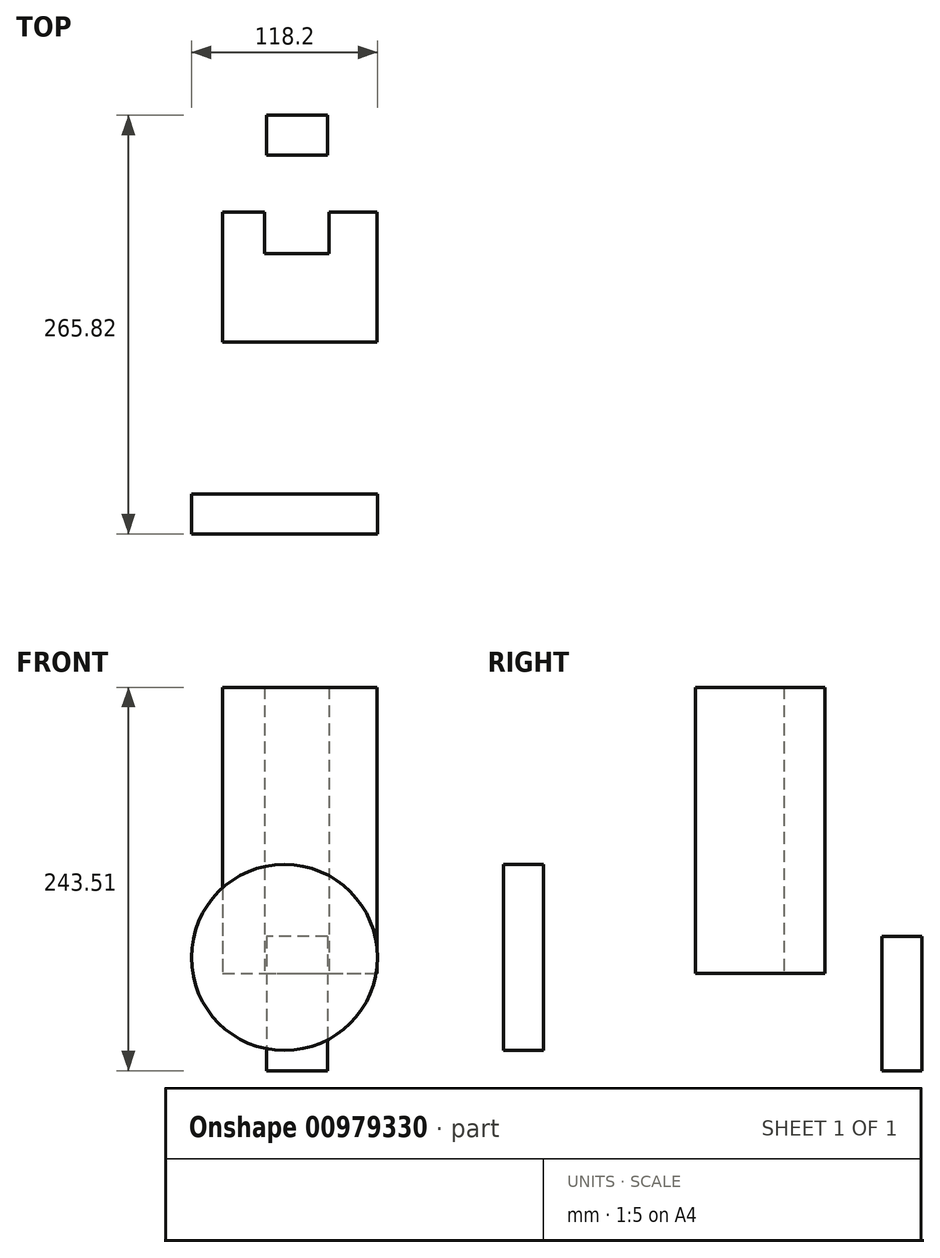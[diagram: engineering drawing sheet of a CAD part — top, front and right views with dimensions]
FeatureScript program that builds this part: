
annotation { "Feature Type Name" : "Feature", "Feature Type Description" : "" }
export const myFeature = defineFeature(function(context is Context, id is Id, definition is map)
    precondition{}
    {
        {
            var Q0;
            Q0=qCreatedBy(makeId("Top.planeOp"),FACE);
            var sketch = newSketch(context, id + "F0", { "sketchPlane" : qUnion([Q0])});
            skLineSegment(sketch, "E0.bottom", {"start": v(-39.24, 38.4) * mm, "end": v(58.8, 38.4) * mm});
            skLineSegment(sketch, "E0.top", {"start": v(-39.24, -43.86) * mm, "end": v(58.8, -43.86) * mm});
            skLineSegment(sketch, "E0.left", {"start": v(-39.24, 38.4) * mm, "end": v(-39.24, -43.86) * mm});
            skLineSegment(sketch, "E0.right", {"start": v(58.8, 38.4) * mm, "end": v(58.8, -43.86) * mm});
            skLineSegment(sketch, "E1.bottom", {"start": v(-12.7, 38.4) * mm, "end": v(28.15, 38.4) * mm});
            skLineSegment(sketch, "E1.top", {"start": v(-12.7, 12.3) * mm, "end": v(28.15, 12.3) * mm});
            skLineSegment(sketch, "E1.left", {"start": v(-12.7, 38.4) * mm, "end": v(-12.7, 12.3) * mm});
            skLineSegment(sketch, "E1.right", {"start": v(28.15, 38.4) * mm, "end": v(28.15, 12.3) * mm});
            skSolve(sketch);
        }
        {
            var Q0;
            Q0=makeQuery(id+"F0.imprint","IMPRINT",FACE,{"disambiguationData":[TD([[makeQuery(id+"F0.imprint","IMPRINT",EDGE,{"derivedFrom":sQuery(id+"F0.wireOp",EDGE,"E0.top")}),1.0]])]});
            extrude(context, id + "F1", {"entities" : qUnion([Q0]), "depth" : 181.6 * mm, "offsetDistance" : 25.4 * mm});
        }
        {
            var Q0;
            Q0=qCreatedBy(makeId("Front.planeOp"),FACE);
            cPlane(context, id + "F2", {"entities" : qUnion([Q0]), "cplaneType" : CPlaneType.OFFSET, "offset" : 100.02 * mm, "oppositeDirection" : true, "width" : 152.4 * mm, "height" : 152.4 * mm});
        }
        {
            var Q0;
            Q0=qCreatedBy(id+"F2.planeOp",FACE);
            var sketch = newSketch(context, id + "F3", { "sketchPlane" : qUnion([Q0])});
            skLineSegment(sketch, "E2.bottom", {"start": v(27.2, 23.32) * mm, "end": v(-11.26, 23.32) * mm});
            skLineSegment(sketch, "E2.top", {"start": v(27.2, -61.9) * mm, "end": v(-11.26, -61.9) * mm});
            skLineSegment(sketch, "E2.left", {"start": v(27.2, 23.32) * mm, "end": v(27.2, -61.9) * mm});
            skLineSegment(sketch, "E2.right", {"start": v(-11.26, 23.32) * mm, "end": v(-11.26, -61.9) * mm});
            skSolve(sketch);
        }
        {
            var Q0;
            Q0=makeQuery(id+"F3.imprint","IMPRINT",FACE,{"disambiguationData":[TD([[makeQuery(id+"F3.imprint","IMPRINT",EDGE,{"derivedFrom":sQuery(id+"F3.wireOp",EDGE,"E2.bottom")}),1.0]])]});
            extrude(context, id + "F4", {"entities" : qUnion([Q0]), "depth" : 25.4 * mm, "offsetDistance" : 25.4 * mm});
        }
        {
            var Q0;
            Q0=qCreatedBy(makeId("Front.planeOp"),FACE);
            cPlane(context, id + "F5", {"entities" : qUnion([Q0]), "cplaneType" : CPlaneType.OFFSET, "offset" : 140.4 * mm, "width" : 152.4 * mm, "height" : 152.4 * mm});
        }
        {
            var Q0;
            Q0=qCreatedBy(id+"F5.planeOp",FACE);
            var sketch = newSketch(context, id + "F6", { "sketchPlane" : qUnion([Q0])});
            skCircle(sketch, "E3", {"center": v(0, 10) * mm, "radius": 59.1 * mm});
            skSolve(sketch);
        }
        {
            var Q0;
            Q0=makeQuery(id+"F6.imprint","IMPRINT",FACE,{"disambiguationData":[TD([[makeQuery(id+"F6.imprint","IMPRINT",EDGE,{"derivedFrom":sQuery(id+"F6.wireOp",EDGE,"E3")}),1.0]])]});
            extrude(context, id + "F7", {"entities" : qUnion([Q0]), "depth" : 25.4 * mm, "offsetDistance" : 25.4 * mm});
        }
    });
